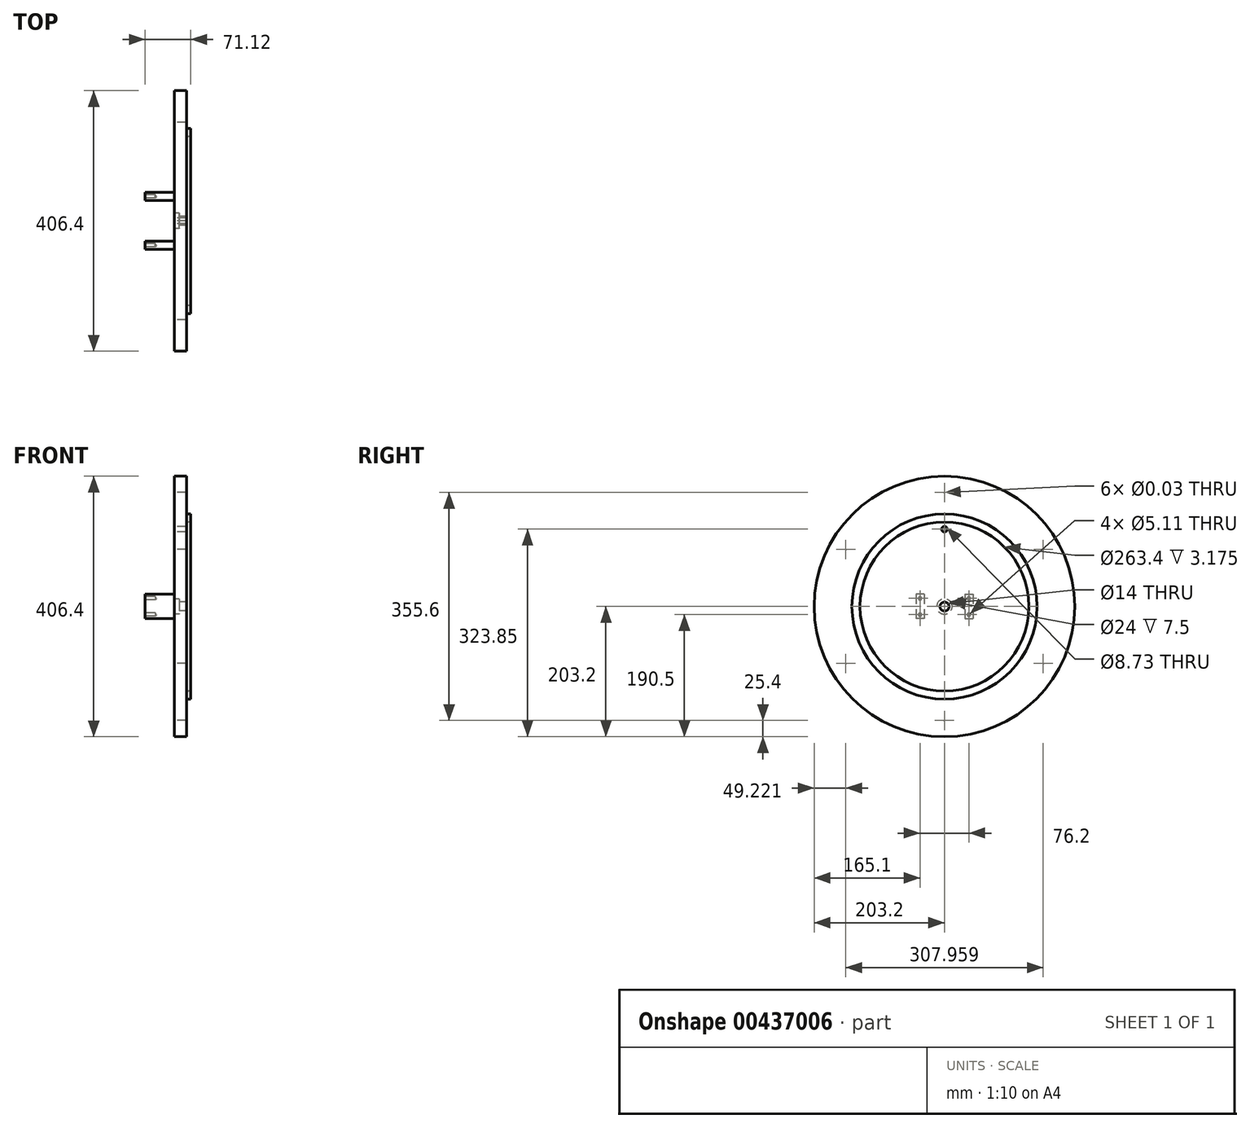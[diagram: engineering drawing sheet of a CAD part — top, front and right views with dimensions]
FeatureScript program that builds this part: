
annotation { "Feature Type Name" : "Feature", "Feature Type Description" : "" }
export const myFeature = defineFeature(function(context is Context, id is Id, definition is map)
    precondition{}
    {
        {
            var Q0;
            Q0=qCreatedBy(makeId("Right.planeOp"),FACE);
            var sketch = newSketch(context, id + "F0", { "sketchPlane" : qUnion([Q0])});
            skCircle(sketch, "E0", {"center": v(0, 0) * mm, "radius": 203.2 * mm});
            skSolve(sketch);
        }
        {
            var Q0;
            Q0 = qSketchRegion(id + "F0", true);
            extrude(context, id + "F1", {"entities" : qUnion([Q0]), "oppositeDirection" : true, "depth" : 19.05 * mm});
        }
        {
            var Q0;
            Q0=makeQuery(id+"F1.opExtrude","CAP_FACE",FACE,{"disambiguationData":[OSD([sQuery(id+"F0.wireOp",EDGE,"E0")])],"isStart":true});
            var sketch = newSketch(context, id + "F2", { "sketchPlane" : qUnion([Q0])});
            skCircle(sketch, "E1", {"center": v(0, 0) * mm, "radius": 144.4 * mm});
            skCircle(sketch, "E2.0", {"center": v(0, 0) * mm, "radius": 131.7 * mm});
            skSolve(sketch);
        }
        {
            var Q0;
            Q0 = qSketchRegion(id + "F2", true);
            extrude(context, id + "F3", {"entities" : qUnion([Q0]), "operationType" : NewBodyOperationType.ADD, "depth" : 6.35 * mm});
        }
        {
            var Q0;
            Q0=makeQuery(id+"F3.opExtrude","CAP_EDGE",EDGE,{"disambiguationData":[OSD([sQuery(id+"F2.wireOp",EDGE,"E2.0")])],"isStart":true});
            fillet(context, id + "F4", {"entities" : qUnion([Q0]), "radius" : 3.17 * mm, "tangentPropagation" : true, "allowEdgeOverflow" : false});
        }
        {
            var Q0;
            Q0=makeQuery(id+"F1.opExtrude","CAP_FACE",FACE,{"disambiguationData":[OSD([sQuery(id+"F0.wireOp",EDGE,"E0")])],"isStart":false});
            var sketch = newSketch(context, id + "F5", { "sketchPlane" : qUnion([Q0])});
            skCircle(sketch, "E3", {"center": v(0, 0) * mm, "radius": 177.8 * mm, "construction": true});
            skLineSegment(sketch, "E4", {"start": v(0, 0) * mm, "end": v(0, 177.8) * mm, "construction": true});
            skPoint(sketch, "E5", {"position": v(0, 177.8) * mm});
            skPoint(sketch, "E6.1.0", {"position": v(-153.98, 88.9) * mm});
            skPoint(sketch, "E6.2.0", {"position": v(-153.98, -88.9) * mm});
            skPoint(sketch, "E6.3.0", {"position": v(0, -177.8) * mm});
            skPoint(sketch, "E6.4.0", {"position": v(153.98, -88.9) * mm});
            skPoint(sketch, "E6.5.0", {"position": v(153.98, 88.9) * mm});
            skSolve(sketch);
        }
        {
            var Q0;
            Q0=sQuery(id+"F5.wireOp",VERTEX,"E5");
            var Q1;
            Q1=sQuery(id+"F5.wireOp",VERTEX,"E6.5.0");
            var Q2;
            Q2=sQuery(id+"F5.wireOp",VERTEX,"E6.1.0");
            var Q3;
            Q3=sQuery(id+"F5.wireOp",VERTEX,"E6.2.0");
            var Q4;
            Q4=sQuery(id+"F5.wireOp",VERTEX,"E6.4.0");
            var Q5;
            Q5=sQuery(id+"F5.wireOp",VERTEX,"E6.3.0");
            var Q6;
            Q6=makeQuery(id+"F1.opExtrude","SWEPT_BODY",BODY,{"disambiguationData":[OSD([sQuery(id+"F0.wireOp",EDGE,"E0")])]});
            hole(context, id + "F6", {"style" : HoleStyle.SIMPLE, "endStyle" : HoleEndStyle.THROUGH, "standardTappedOrClearance" : lookupTablePath({ "standard" : "ANSI", "size" : "7/8", "type" : "Drilled" }), "standardBlindInLast" : lookupTablePath({ "standard" : "ANSI", "size" : "7/8", "type" : "Drilled" }), "holeDiameter" : 7 / 203.2 * mm, "isTappedThrough" : true, "tappedDepth" : 24.13 * mm, "tapClearance" : 3, "startFromSketch" : true, "locations" : qUnion([Q0, Q1, Q2, Q3, Q4, Q5]), "scope" : qUnion([Q6])});
        }
        {
            var Q0;
            Q0=makeQuery(id+"F1.opExtrude","CAP_FACE",FACE,{"disambiguationData":[OSD([sQuery(id+"F0.wireOp",EDGE,"E0")])],"isStart":false});
            var sketch = newSketch(context, id + "F7", { "sketchPlane" : qUnion([Q0])});
            skPoint(sketch, "E7", {"position": v(0, 0) * mm});
            skSolve(sketch);
        }
        {
            var Q0;
            Q0=sQuery(id+"F7.wireOp",VERTEX,"E7");
            var Q1;
            Q1=makeQuery(id+"F1.opExtrude","SWEPT_BODY",BODY,{"disambiguationData":[OSD([sQuery(id+"F0.wireOp",EDGE,"E0")])]});
            hole(context, id + "F8", {"style" : HoleStyle.C_BORE, "endStyle" : HoleEndStyle.THROUGH, "standardTappedOrClearance" : lookupTablePath({ "standard" : "ISO", "size" : "14", "type" : "Drilled" }), "standardBlindInLast" : lookupTablePath({ "standard" : "ISO", "size" : "14", "type" : "Drilled" }), "holeDiameter" : 14 * mm, "cBoreDiameter" : 24 * mm, "cBoreDepth" : 7.5 * mm, "isTappedThrough" : true, "tappedDepth" : 24.13 * mm, "tapClearance" : 3, "startFromSketch" : true, "locations" : qUnion([Q0]), "scope" : qUnion([Q1])});
        }
        {
            var Q0;
            Q0=makeQuery(id+"F1.opExtrude","CAP_FACE",FACE,{"disambiguationData":[OSD([sQuery(id+"F0.wireOp",EDGE,"E0")])],"isStart":false});
            var sketch = newSketch(context, id + "F9", { "sketchPlane" : qUnion([Q0])});
            skLineSegment(sketch, "E8", {"start": v(0, 230.66) * mm, "end": v(0, -260.99) * mm, "construction": true});
            skLineSegment(sketch, "E9", {"start": v(-300.12, 0) * mm, "end": v(294.62, 0) * mm, "construction": true});
            skLineSegment(sketch, "E10.0", {"start": v(31.75, 19.05) * mm, "end": v(31.75, -19.05) * mm});
            skLineSegment(sketch, "E11.0", {"start": v(44.45, 19.05) * mm, "end": v(44.45, -19.05) * mm});
            skLineSegment(sketch, "E12.MirrorCS", {"start": v(31.75, 19.05) * mm, "end": v(44.45, 19.05) * mm});
            skPoint(sketch, "E13.orphan", {"position": v(-300.12, 19.05) * mm});
            skPoint(sketch, "E14.orphan", {"position": v(294.62, 19.05) * mm});
            skPoint(sketch, "E15.orphan", {"position": v(294.62, -19.05) * mm});
            skLineSegment(sketch, "E16.trimOffspring", {"start": v(31.75, -19.05) * mm, "end": v(44.45, -19.05) * mm});
            skPoint(sketch, "E17.0.start.orphan", {"position": v(-300.12, -19.05) * mm});
            skLineSegment(sketch, "E18.MirrorCS", {"start": v(-31.75, -19.05) * mm, "end": v(-44.45, -19.05) * mm});
            skLineSegment(sketch, "E19.MirrorCS", {"start": v(-31.75, 19.05) * mm, "end": v(-44.45, 19.05) * mm});
            skLineSegment(sketch, "E20.MirrorCS", {"start": v(-44.45, 19.05) * mm, "end": v(-44.45, -19.05) * mm});
            skLineSegment(sketch, "E21.MirrorCS", {"start": v(-31.75, 19.05) * mm, "end": v(-31.75, -19.05) * mm});
            skSolve(sketch);
        }
        {
            var Q0;
            Q0 = qSketchRegion(id + "F9", true);
            extrude(context, id + "F10", {"entities" : qUnion([Q0]), "operationType" : NewBodyOperationType.ADD, "depth" : 45.72 * mm});
        }
        {
            var Q0;
            Q0=makeQuery(id+"F10.opExtrude","CAP_FACE",FACE,{"disambiguationData":[OSD([sQuery(id+"F9.wireOp",EDGE,"E18.MirrorCS"),sQuery(id+"F9.wireOp",EDGE,"E19.MirrorCS"),sQuery(id+"F9.wireOp",EDGE,"E20.MirrorCS"),sQuery(id+"F9.wireOp",EDGE,"E21.MirrorCS")])],"isStart":false});
            var sketch = newSketch(context, id + "F11", { "sketchPlane" : qUnion([Q0])});
            skLineSegment(sketch, "E22", {"start": v(-263.32, 0) * mm, "end": v(261.83, 0) * mm, "construction": true});
            skLineSegment(sketch, "E23.0", {"start": v(-263.32, -12.7) * mm, "end": v(261.83, -12.7) * mm, "construction": true});
            skLineSegment(sketch, "E24", {"start": v(-38.1, -19.05) * mm, "end": v(-38.1, 29.34) * mm, "construction": true});
            skLineSegment(sketch, "E25", {"start": v(0, -77.63) * mm, "end": v(0, 57.63) * mm, "construction": true});
            skPoint(sketch, "E26", {"position": v(-38.1, -12.7) * mm});
            skPoint(sketch, "E27", {"position": v(-86.2, 49.38) * mm});
            skPoint(sketch, "E28.MirrorP", {"position": v(-38.1, 12.7) * mm});
            skPoint(sketch, "E29.MirrorP", {"position": v(38.1, 12.7) * mm});
            skPoint(sketch, "E30.MirrorP", {"position": v(38.1, -12.7) * mm});
            skSolve(sketch);
        }
        {
            var Q0;
            Q0=sQuery(id+"F11.wireOp",VERTEX,"E28.MirrorP");
            var Q1;
            Q1=sQuery(id+"F11.wireOp",VERTEX,"E26");
            var Q2;
            Q2=sQuery(id+"F11.wireOp",VERTEX,"E29.MirrorP");
            var Q3;
            Q3=sQuery(id+"F11.wireOp",VERTEX,"E30.MirrorP");
            var Q4;
            Q4=makeQuery(id+"F1.opExtrude","SWEPT_BODY",BODY,{"disambiguationData":[OSD([sQuery(id+"F0.wireOp",EDGE,"E0")])]});
            hole(context, id + "F12", {"style" : HoleStyle.SIMPLE, "endStyle" : HoleEndStyle.BLIND, "standardTappedOrClearance" : lookupTablePath({ "standard" : "ANSI", "engagement" : "75%", "pitch" : "20 tpi", "size" : "1/4", "type" : "Tapped" }), "standardBlindInLast" : lookupTablePath({ "standard" : "ANSI", "engagement" : "75%", "pitch" : "20 tpi", "size" : "1/4", "type" : "Tapped" }), "holeDiameter" : 5.1 * mm, "showTappedDepth" : true, "holeDepth" : 15.88 * mm, "isTappedThrough" : true, "tappedDepth" : 12.06 * mm, "tapClearance" : 3, "startFromSketch" : true, "locations" : qUnion([Q0, Q1, Q2, Q3]), "scope" : qUnion([Q4]), "majorDiameter" : 6.35 * mm});
        }
        {
            var Q0;
            Q0=makeQuery(id+"F1.opExtrude","CAP_FACE",FACE,{"disambiguationData":[OSD([sQuery(id+"F0.wireOp",EDGE,"E0")])],"isStart":false});
            var sketch = newSketch(context, id + "F13", { "sketchPlane" : qUnion([Q0])});
            skLineSegment(sketch, "E31", {"start": v(-299.89, 0) * mm, "end": v(268.24, 0) * mm, "construction": true});
            skLineSegment(sketch, "E32", {"start": v(0, 262.21) * mm, "end": v(0, -264.47) * mm, "construction": true});
            skLineSegment(sketch, "E33.0", {"start": v(-299.89, 120.65) * mm, "end": v(268.24, 120.65) * mm, "construction": true});
            skPoint(sketch, "E34", {"position": v(0, 120.65) * mm});
            skSolve(sketch);
        }
        {
            var Q0;
            Q0=sQuery(id+"F13.wireOp",VERTEX,"E34");
            var Q1;
            Q1=makeQuery(id+"F1.opExtrude","SWEPT_BODY",BODY,{"disambiguationData":[OSD([sQuery(id+"F0.wireOp",EDGE,"E0")])]});
            hole(context, id + "F14", {"style" : HoleStyle.SIMPLE, "endStyle" : HoleEndStyle.THROUGH, "holeDiameter" : 8.73 * mm, "isTappedThrough" : true, "tappedDepth" : 12.06 * mm, "tapClearance" : 3, "startFromSketch" : true, "locations" : qUnion([Q0]), "scope" : qUnion([Q1])});
        }
    });
